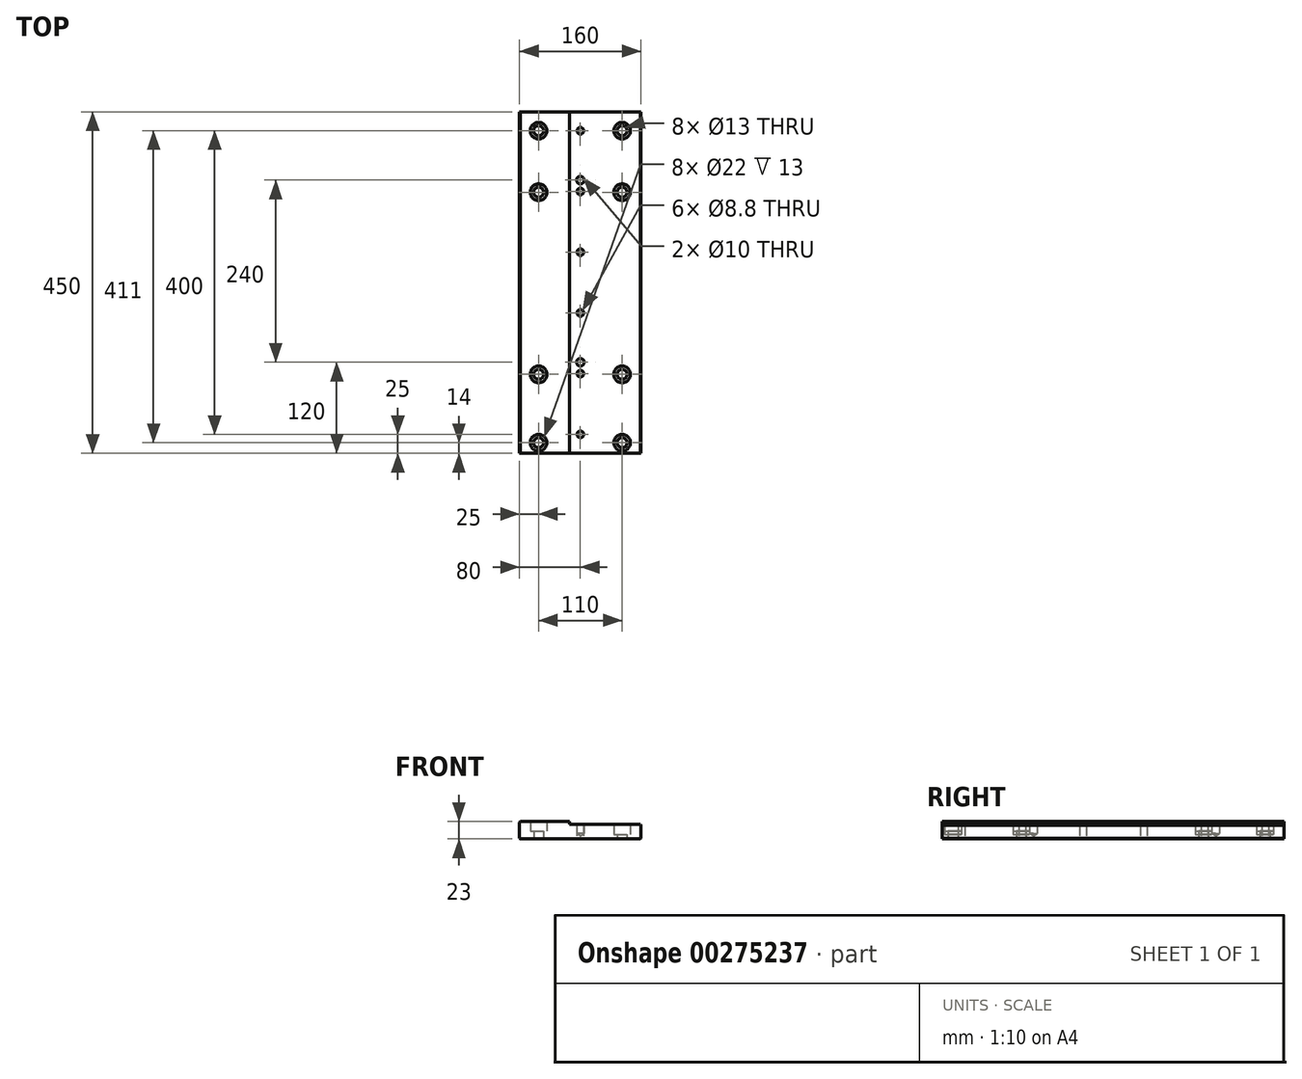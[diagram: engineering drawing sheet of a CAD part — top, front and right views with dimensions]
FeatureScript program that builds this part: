
annotation { "Feature Type Name" : "Feature", "Feature Type Description" : "" }
export const myFeature = defineFeature(function(context is Context, id is Id, definition is map)
    precondition{}
    {
        {
            var Q0;
            Q0=qCreatedBy(makeId("Front.planeOp"),FACE);
            var sketch = newSketch(context, id + "F0", { "sketchPlane" : qUnion([Q0])});
            skLineSegment(sketch, "E0", {"start": v(0, 0) * mm, "end": v(0, 4) * mm});
            skLineSegment(sketch, "E1", {"start": v(0, 4) * mm, "end": v(-66, 4) * mm});
            skLineSegment(sketch, "E2", {"start": v(-66, 4) * mm, "end": v(-66, -19) * mm});
            skLineSegment(sketch, "E3", {"start": v(-66, -19) * mm, "end": v(94, -19) * mm});
            skLineSegment(sketch, "E4", {"start": v(94, -19) * mm, "end": v(94, 0) * mm});
            skLineSegment(sketch, "E5", {"start": v(94, 0) * mm, "end": v(0, 0) * mm});
            skSolve(sketch);
        }
        {
            var Q0;
            Q0 = qSketchRegion(id + "F0", true);
            extrude(context, id + "F1", {"entities" : qUnion([Q0]), "oppositeDirection" : true, "depth" : 450 * mm});
        }
        {
            var Q0;
            Q0=makeQuery(id+"F1.opExtrude","SWEPT_FACE",FACE,{"disambiguationData":[OSD([sQuery(id+"F0.wireOp",EDGE,"E1")])]});
            var sketch = newSketch(context, id + "F2", { "sketchPlane" : qUnion([Q0])});
            skLineSegment(sketch, "E6", {"start": v(-41, 505.46) * mm, "end": v(-41, -94.91) * mm, "construction": true});
            skLineSegment(sketch, "E7", {"start": v(69, 511.26) * mm, "end": v(69, -86.44) * mm, "construction": true});
            skCircle(sketch, "E8", {"center": v(-41, 425) * mm, "radius": 14.6 * mm});
            skCircle(sketch, "E9", {"center": v(69, 425) * mm, "radius": 15.87 * mm});
            skCircle(sketch, "E10", {"center": v(-41, 344) * mm, "radius": 15.03 * mm});
            skCircle(sketch, "E11", {"center": v(69, 344) * mm, "radius": 16.78 * mm});
            skCircle(sketch, "E12", {"center": v(-41, 104) * mm, "radius": 21.8 * mm});
            skCircle(sketch, "E13", {"center": v(69, 104) * mm, "radius": 18.43 * mm});
            skCircle(sketch, "E14", {"center": v(-41, 14) * mm, "radius": 20.98 * mm});
            skCircle(sketch, "E15", {"center": v(69, 14) * mm, "radius": 20.45 * mm});
            skSolve(sketch);
        }
        {
            var Q0;
            Q0=sQuery(id+"F2.wireOp",VERTEX,"E8.center");
            var Q1;
            Q1=sQuery(id+"F2.wireOp",VERTEX,"E10.center");
            var Q2;
            Q2=sQuery(id+"F2.wireOp",VERTEX,"E12.center");
            var Q3;
            Q3=sQuery(id+"F2.wireOp",VERTEX,"E14.center");
            var Q4;
            Q4=makeQuery(id+"F1.opExtrude","SWEPT_BODY",BODY,{"disambiguationData":[OSD([sQuery(id+"F0.wireOp",EDGE,"E0"),sQuery(id+"F0.wireOp",EDGE,"E1"),sQuery(id+"F0.wireOp",EDGE,"E2"),sQuery(id+"F0.wireOp",EDGE,"E3"),sQuery(id+"F0.wireOp",EDGE,"E4"),sQuery(id+"F0.wireOp",EDGE,"E5")])]});
            hole(context, id + "F3", {"style" : HoleStyle.C_BORE, "endStyle" : HoleEndStyle.BLIND, "holeDiameter" : 13 * mm, "cBoreDiameter" : 22 * mm, "cBoreDepth" : 13 * mm, "holeDepth" : 25 * mm, "tappedDepth" : 12 * mm, "tapClearance" : 3, "startFromSketch" : true, "locations" : qUnion([Q0, Q1, Q2, Q3]), "scope" : qUnion([Q4])});
        }
        {
            var Q0;
            Q0=makeQuery(id+"F1.opExtrude","SWEPT_FACE",FACE,{"disambiguationData":[OSD([sQuery(id+"F0.wireOp",EDGE,"E5")])]});
            var sketch = newSketch(context, id + "F4", { "sketchPlane" : qUnion([Q0])});
            skCircle(sketch, "E16.0", {"center": v(69, 425) * mm, "radius": 15.87 * mm});
            skCircle(sketch, "E17.0", {"center": v(69, 344) * mm, "radius": 16.78 * mm});
            skCircle(sketch, "E18.0", {"center": v(69, 104) * mm, "radius": 18.43 * mm});
            skCircle(sketch, "E19.0", {"center": v(69, 14) * mm, "radius": 20.45 * mm});
            skLineSegment(sketch, "E20", {"start": v(14, 490.33) * mm, "end": v(14, -113.23) * mm, "construction": true});
            skSolve(sketch);
        }
        {
            var Q0;
            Q0=sQuery(id+"F4.wireOp",VERTEX,"E16.0.center");
            var Q1;
            Q1=sQuery(id+"F4.wireOp",VERTEX,"E17.0.center");
            var Q2;
            Q2=sQuery(id+"F4.wireOp",VERTEX,"E18.0.center");
            var Q3;
            Q3=sQuery(id+"F4.wireOp",VERTEX,"E19.0.center");
            var Q4;
            Q4=makeQuery(id+"F1.opExtrude","SWEPT_BODY",BODY,{"disambiguationData":[OSD([sQuery(id+"F0.wireOp",EDGE,"E0"),sQuery(id+"F0.wireOp",EDGE,"E1"),sQuery(id+"F0.wireOp",EDGE,"E2"),sQuery(id+"F0.wireOp",EDGE,"E3"),sQuery(id+"F0.wireOp",EDGE,"E4"),sQuery(id+"F0.wireOp",EDGE,"E5")])]});
            hole(context, id + "F5", {"style" : HoleStyle.C_BORE, "endStyle" : HoleEndStyle.BLIND, "holeDiameter" : 13 * mm, "cBoreDiameter" : 22 * mm, "cBoreDepth" : 13 * mm, "holeDepth" : 25 * mm, "tappedDepth" : 12 * mm, "tapClearance" : 3, "startFromSketch" : true, "locations" : qUnion([Q0, Q1, Q2, Q3]), "scope" : qUnion([Q4])});
        }
        {
            var Q0;
            Q0=makeQuery(id+"F1.opExtrude","SWEPT_FACE",FACE,{"disambiguationData":[OSD([sQuery(id+"F0.wireOp",EDGE,"E5")])]});
            var sketch = newSketch(context, id + "F6", { "sketchPlane" : qUnion([Q0])});
            skLineSegment(sketch, "E21", {"start": v(14, -85.34) * mm, "end": v(14, 484.5) * mm, "construction": true});
            skCircle(sketch, "E22", {"center": v(14, 25) * mm, "radius": 6.97 * mm});
            skCircle(sketch, "E23", {"center": v(14, 105) * mm, "radius": 8.39 * mm});
            skCircle(sketch, "E24", {"center": v(14, 185) * mm, "radius": 10.82 * mm});
            skCircle(sketch, "E25", {"center": v(14, 265) * mm, "radius": 10.2 * mm});
            skCircle(sketch, "E26", {"center": v(14, 345) * mm, "radius": 8.08 * mm});
            skCircle(sketch, "E27", {"center": v(14, 425) * mm, "radius": 9.63 * mm});
            skCircle(sketch, "E28", {"center": v(14, 120) * mm, "radius": 10.74 * mm});
            skCircle(sketch, "E29", {"center": v(14, 360) * mm, "radius": 11.28 * mm});
            skSolve(sketch);
        }
        {
            var Q0;
            Q0=sQuery(id+"F6.wireOp",VERTEX,"E22.center");
            var Q1;
            Q1=sQuery(id+"F6.wireOp",VERTEX,"E23.center");
            var Q2;
            Q2=sQuery(id+"F6.wireOp",VERTEX,"E24.center");
            var Q3;
            Q3=sQuery(id+"F6.wireOp",VERTEX,"E25.center");
            var Q4;
            Q4=sQuery(id+"F6.wireOp",VERTEX,"E26.center");
            var Q5;
            Q5=sQuery(id+"F6.wireOp",VERTEX,"E27.center");
            var Q6;
            Q6=makeQuery(id+"F1.opExtrude","SWEPT_BODY",BODY,{"disambiguationData":[OSD([sQuery(id+"F0.wireOp",EDGE,"E0"),sQuery(id+"F0.wireOp",EDGE,"E1"),sQuery(id+"F0.wireOp",EDGE,"E2"),sQuery(id+"F0.wireOp",EDGE,"E3"),sQuery(id+"F0.wireOp",EDGE,"E4"),sQuery(id+"F0.wireOp",EDGE,"E5")])]});
            hole(context, id + "F7", {"style" : HoleStyle.SIMPLE, "endStyle" : HoleEndStyle.BLIND, "standardTappedOrClearance" : lookupTablePath({ "standard" : "ISO", "fit" : "Normal", "size" : "M8", "type" : "Clearance" }), "standardBlindInLast" : lookupTablePath({ "fit" : "Standard", "standard" : "ISO", "size" : "M8", "type" : "Clearance" }), "holeDiameter" : 8.8 * mm, "holeDepth" : 25 * mm, "tappedDepth" : 12 * mm, "tapClearance" : 3, "startFromSketch" : true, "locations" : qUnion([Q0, Q1, Q2, Q3, Q4, Q5]), "scope" : qUnion([Q6])});
        }
        {
            var Q0;
            Q0=sQuery(id+"F6.wireOp",VERTEX,"E28.center");
            var Q1;
            Q1=sQuery(id+"F6.wireOp",VERTEX,"E29.center");
            var Q2;
            Q2=makeQuery(id+"F1.opExtrude","SWEPT_BODY",BODY,{"disambiguationData":[OSD([sQuery(id+"F0.wireOp",EDGE,"E0"),sQuery(id+"F0.wireOp",EDGE,"E1"),sQuery(id+"F0.wireOp",EDGE,"E2"),sQuery(id+"F0.wireOp",EDGE,"E3"),sQuery(id+"F0.wireOp",EDGE,"E4"),sQuery(id+"F0.wireOp",EDGE,"E5")])]});
            hole(context, id + "F8", {"style" : HoleStyle.SIMPLE, "endStyle" : HoleEndStyle.BLIND, "holeDiameter" : 10 * mm, "holeDepth" : 12 * mm, "tappedDepth" : 12 * mm, "tapClearance" : 3, "startFromSketch" : true, "locations" : qUnion([Q0, Q1]), "scope" : qUnion([Q2])});
        }
        {
            var Q0;
            Q0=makeQuery(id+"F1.opExtrude","SWEPT_EDGE",EDGE,{"disambiguationData":[OSD([sQuery(id+"F0.wireOp",EDGE,"E4"),sQuery(id+"F0.wireOp",EDGE,"E5")])]});
            var Q1;
            Q1=makeQuery(id+"F1.opExtrude","SWEPT_EDGE",EDGE,{"disambiguationData":[OSD([sQuery(id+"F0.wireOp",EDGE,"E1"),sQuery(id+"F0.wireOp",EDGE,"E2")])]});
            var Q2;
            Q2=makeQuery(id+"F1.opExtrude","SWEPT_EDGE",EDGE,{"disambiguationData":[OSD([sQuery(id+"F0.wireOp",EDGE,"E3"),sQuery(id+"F0.wireOp",EDGE,"E4")])]});
            var Q3;
            Q3=makeQuery(id+"F1.opExtrude","SWEPT_EDGE",EDGE,{"disambiguationData":[OSD([sQuery(id+"F0.wireOp",EDGE,"E2"),sQuery(id+"F0.wireOp",EDGE,"E3")])]});
            chamfer(context, id + "F9", {"entities" : qUnion([Q0, Q1, Q2, Q3]), "chamferType" : ChamferType.OFFSET_ANGLE, "width" : 1 * mm, "oppositeDirection" : false, "angle" : 45 * degree, "tangentPropagation" : true});
        }
    });
